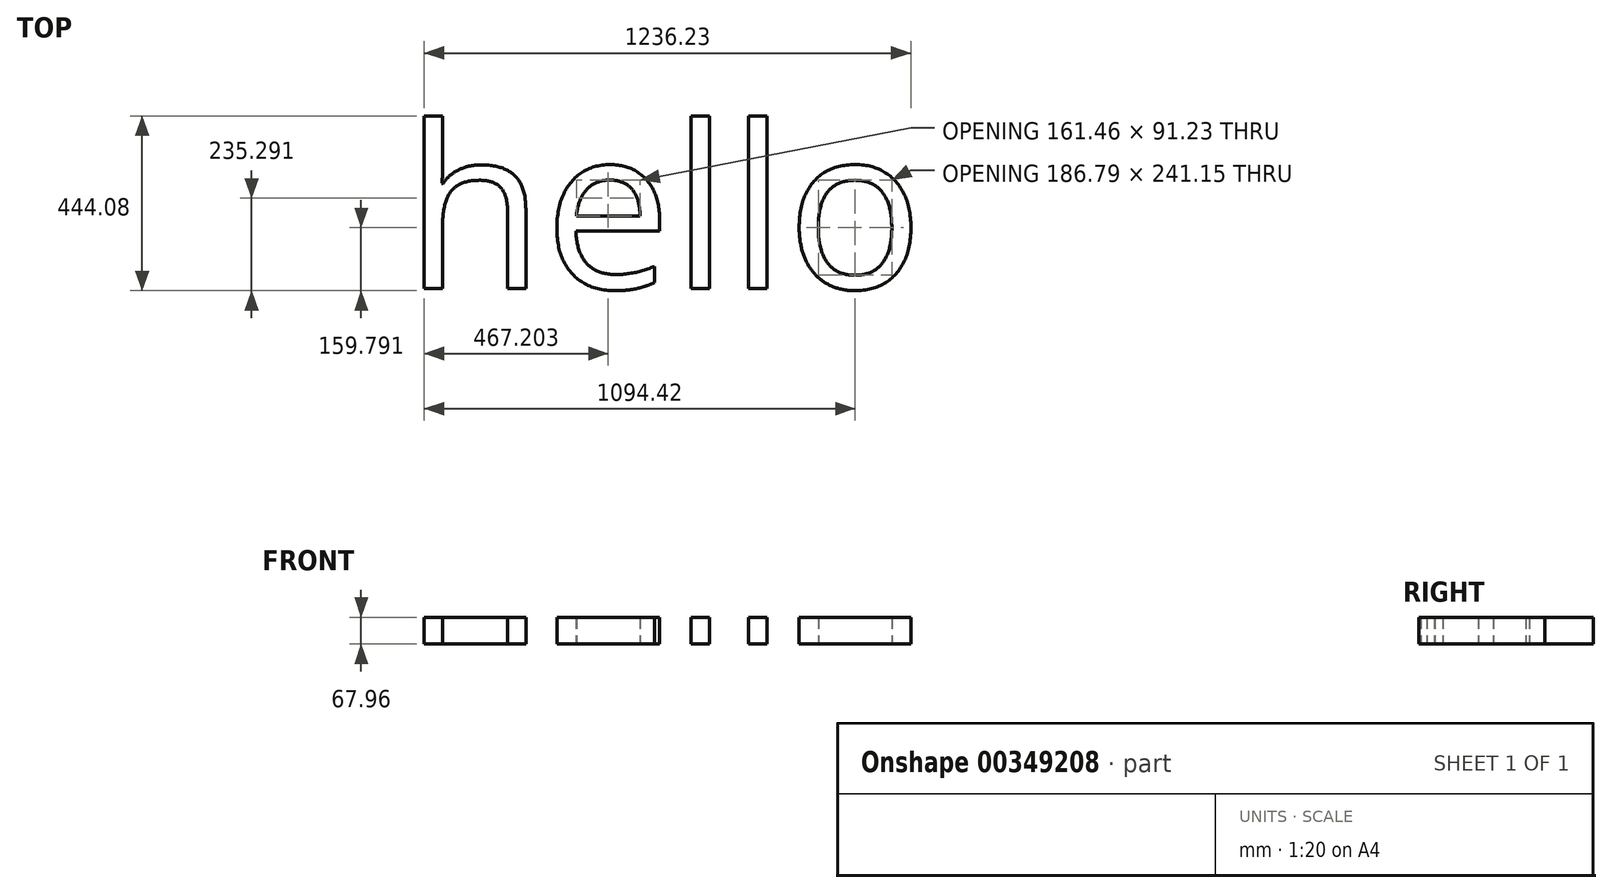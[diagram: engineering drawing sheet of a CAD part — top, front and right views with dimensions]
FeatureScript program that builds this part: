
annotation { "Feature Type Name" : "Feature", "Feature Type Description" : "" }
export const myFeature = defineFeature(function(context is Context, id is Id, definition is map)
    precondition{}
    {
        {
            var Q0;
            Q0=qCreatedBy(makeId("Top.planeOp"),FACE);
            var sketch = newSketch(context, id + "F0", { "sketchPlane" : qUnion([Q0])});
            skText(sketch, "E0", { "text": "hello", "fontName": "OpenSans-Regular.ttf"});
            const initialGuessF0  = {"E0": [0.0117, -0.41541, 1, 0, 0.41541]};
            skSetInitialGuess(sketch, initialGuessF0);
            skSolve(sketch);
        }
        {
            var Q0;
            Q0 = qSketchRegion(id + "F0", true);
            extrude(context, id + "F1", {"entities" : qUnion([Q0]), "depth" : 67.96 * mm});
        }
    });
